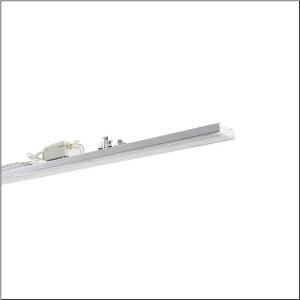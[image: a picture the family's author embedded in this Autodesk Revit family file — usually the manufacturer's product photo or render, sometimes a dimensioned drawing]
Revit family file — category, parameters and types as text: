
# Revit family: licross_r__11_recessed_mo_51tl12dn4axg_bf66
name_source: partatom
category: Lighting Fixtures
units: mm (PartAtom-declared; Revit-internal decimal feet)

## family parameters
Cut with Voids When Loaded = No
Host = Face
Light Source = No
Part Type = Normal
Room Calculation Point = No
Round Connector Dimension = Use Diameter
Shared = No

## types (1)
- --- (1 x LED, 10240 lm, 56.7 W, 4000K)
    Apparent Load = 57 VA
    CIE Flux Codes = 67 92 99 100 100
    Color Rendering = 80
    Color Temperature = 4000K
    Default Elevation = 1800 mm
    Description = Licross® 11 Recessed MO, luminaire insert, of sheet steel, coil coated, white, length: 1.500mm, width: 66mm, height: 67mm, LED rated luminous flux: 10.240lm, light colour: 840, control gear: DALI 2, with plug, 5-pole, with phase selection, mains connection: 220..240V, AC, 50/60Hz, rated input power: 57W, halogen-free wiring, primary optical cover: cover, of PMMA, light emission: direct distribution, primary light characteristic: symmetric, protection rating (complete): IP40, insulation class (complete): insulation class I (protective earthing), certification: CE, ENEC, VDE, UKCA, protection symbol: D if used in an environment without relevant dust loads with corresponding accessories, impact resistance: IK06, permissible ambient temperature for indoor applications: -25..+35°C, corresponds to IFS (International Featured Standards) requirements for safety and quality in the food industry, reducing of maximum allowable ambient temperature of 5°C with ceiling mounting, LABS conformity tested according to VDMA 24364:2018-05, packaging unit: 1 piece
    Height = 58 mm
    Lamp = 1 x LED
    Lamp Light Flux = 10240 lm
    Lamp Power = 56.7 W
    Lamp count = 1
    Length = 1500 mm
    Luminous efficacy = 181 lm/W
    Manufacturer = Siteco
    ModVariant = No
    Model = 51TL12DN4AXG
    Mounting Place = Ceiling
    Mounting Type = Pendant
    Number of Poles = 1
    OnlyDefault = Yes
    Power Factor = 1
    Product Name = Licross® 11 Recessed MO
    Product group = luminaire insert
    ProductGroupID = 901
    Protection Class = Protection class I
    Protection Degree = IP 40
    RLX_Detail_Level = 1
    RLX_Emergency_Light_Flux = 0 lm
    RLX_Emergency_Type = 0
    RLX_Emergency_Type_DB = No
    RlxData = <blob elided: 24321 chars, md5=20fec709>
    Socket = socket
    Standby Power = 0 W
    System Light Flux = 10240 lm
    System Power = 57 W
    Type Comments = factory setting: luminous flux: 100 % | dim-lin: 254 | 378 mA
    Type Image = l_1296930.jpg
    URL = http://relux.com
    VarID = @adj_095622
    Voltage = 0 V
    Weight = 0.00 kg
    Width = 66 mm

## geometry (parser evidence)
native form markers: Blend x4, Sweep x11
no freeform markers — native parametric forms only
